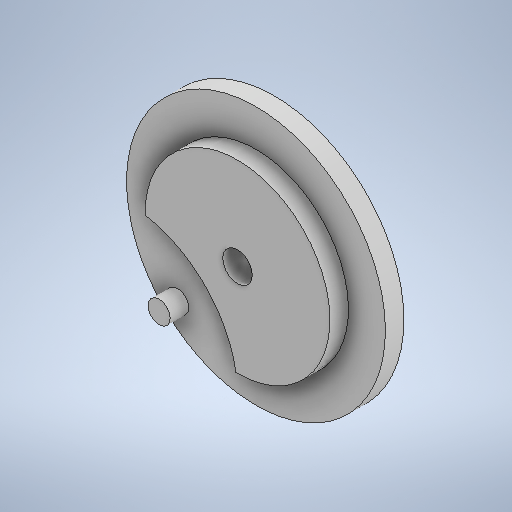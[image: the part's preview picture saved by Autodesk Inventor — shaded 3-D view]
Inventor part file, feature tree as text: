
AUTODESK INVENTOR PART (.ipt)
format: ipt  version: 2025.2 (Build 292293000, 293)  size: 254,976 bytes
history: native  units: mm
features: extrude x2, sketch x1
ambient origin geometry x8: Origin, YZ Plane, XZ Plane, XY Plane, X Axis, Y Axis, Z Axis, Center Point
bodies: Solid1 (feature_tree)
feature tree (3):
  sketch  "Sketch1"  dims[d0=30.0mm d1=30.0mm d2=60.0mm d3=60.0mm d4=70.0mm d5=50.0mm d6=8.0mm d7=6.0mm d8=5.0mm d9=0.0mm d10=5.0mm d11=0.0mm]
  extrude  "Extrusion1"  Depth=30.0mm
  extrude  "Extrusion2"  Depth=5.0mm
